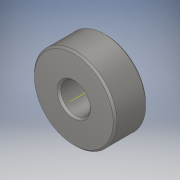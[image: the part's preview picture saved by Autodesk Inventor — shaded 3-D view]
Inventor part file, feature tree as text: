
AUTODESK INVENTOR PART (.ipt)
format: ipt  version: 2019.4 (Build 234330000, 330)  size: 121,344 bytes
history: native  units: in
note: dims shown in document units (in); Inventor stores cm internally (conversion verified against a paired STEP export)
features: plane x2, extrude x1, chamfer x1, sketch x1
ambient origin geometry x8: Origin, YZ Plane, XZ Plane, XY Plane, X Axis, Y Axis, Z Axis, Center Point
bodies: Solid1 (feature_tree)
feature tree (5):
  extrude  "Extrusion1"  Depth=0.3438in TaperAngle=45.0deg
  chamfer  "Chamfer1"  Distance=0.3125in
  plane  "Work Plane1"
  plane  "Work Plane2"
  sketch  "Sketch1"  dims[d2=0.3438in d3=0.0in d4=0.02in d5=0.125in d6=45.0deg d7=0.3125in d8=0.875in]
